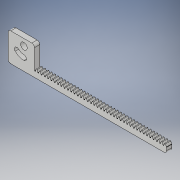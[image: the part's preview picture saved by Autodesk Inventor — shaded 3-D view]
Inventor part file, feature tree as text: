
AUTODESK INVENTOR PART (.ipt)
format: ipt  version: 2019 (Build 230136000, 136)  size: 343,552 bytes
history: native  units: in
note: dims shown in document units (in); Inventor stores cm internally (conversion verified against a paired STEP export)
features: extrude x3, sketch x3, pattern_linear x1, fillet x1
ambient origin geometry x8: Origin, YZ Plane, XZ Plane, XY Plane, X Axis, Y Axis, Z Axis, Center Point
bodies: Solid1 (feature_tree)
feature tree (8):
  extrude  "Extrusion1"  Depth=0.8474in
  extrude  "Extrusion2"  Depth=0.1495in
  extrude  "Extrusion4"  Depth=0.2362in
  pattern_linear  "Rectangular Pattern1"  Spacing1=0.4724in  [1 undecoded]
  fillet  "Fillet1"  Radius=0.1575in
  sketch  "Sketch1"  dims[d0=0.1575in d1=0.0in d3=0.8474in]
  sketch  "Sketch2"  dims[d4=0.1969in d5=0.1495in]
  sketch  "Sketch6"  dims[d7=0.1495in d8=0.5906in d9=0.4724in d10=0.1575in d11=0.0in d12=0.0787in d26=4.7244in d28=0.1969in d49=0.3937in d50=0.0in d53=15.748in d55=0.0982in d57=0.0071in d58=0.0708in d59=0.0104in d60=0.0263in d61=0.0878in d63=0.7874in d64=0.2362in]
note: 1 required parameter value undecoded (feature->parameter linkage not recoverable at this tier; creation-order binding heuristic only, values carry confidence <= 0.55)
